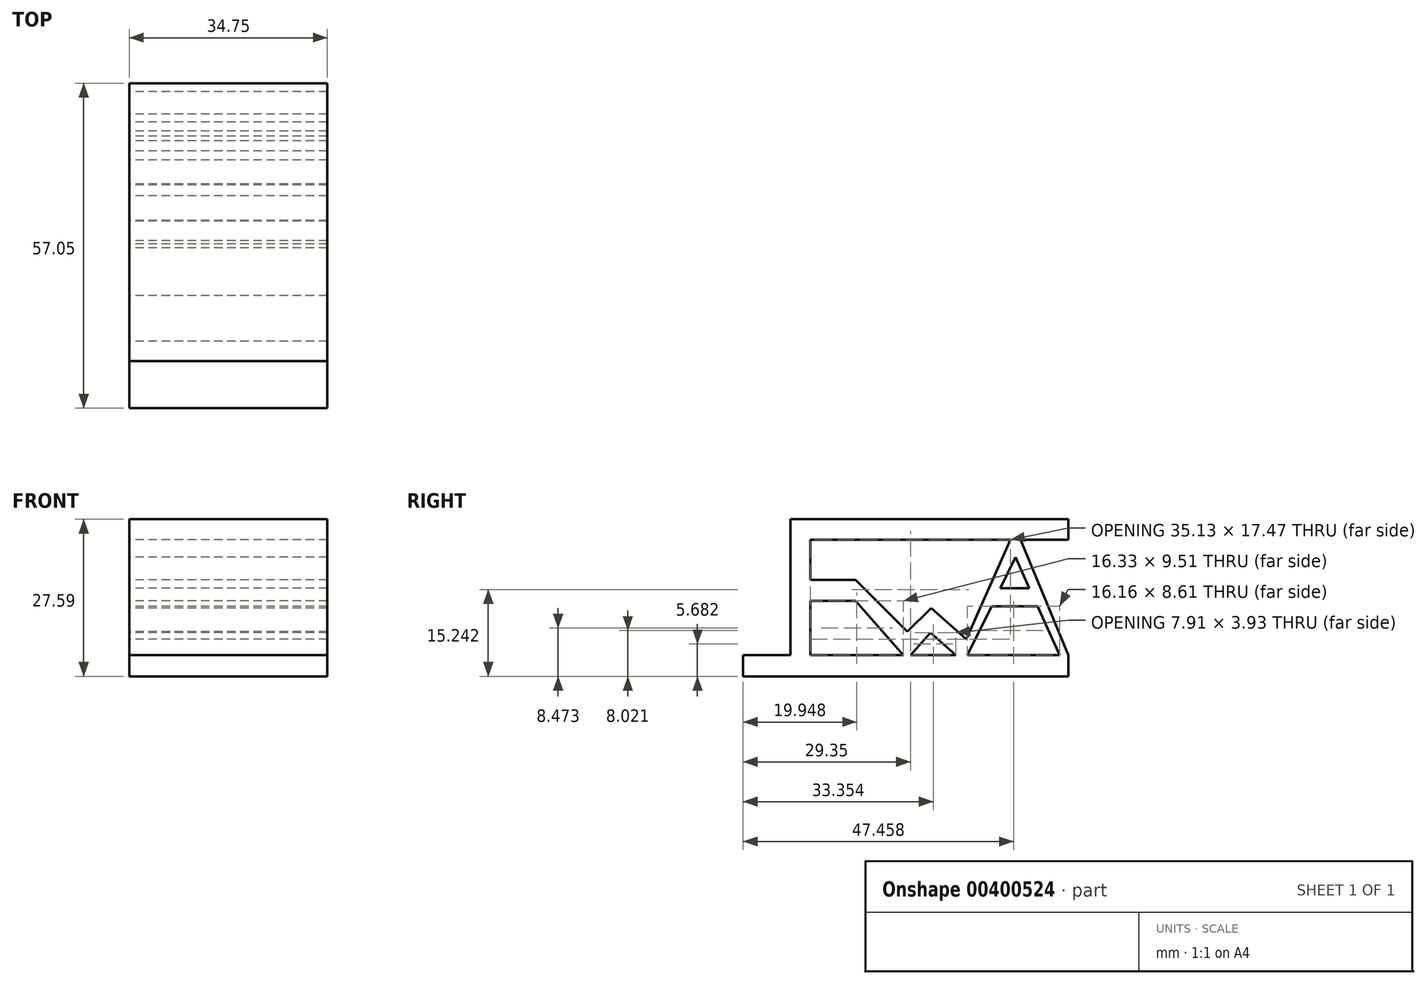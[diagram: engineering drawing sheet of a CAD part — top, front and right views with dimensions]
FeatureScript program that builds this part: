
annotation { "Feature Type Name" : "Feature", "Feature Type Description" : "" }
export const myFeature = defineFeature(function(context is Context, id is Id, definition is map)
    precondition{}
    {
        {
            var Q0;
            Q0=qCreatedBy(makeId("Right.planeOp"),FACE);
            var sketch = newSketch(context, id + "F0", { "sketchPlane" : qUnion([Q0])});
            skLineSegment(sketch, "E0.left", {"start": v(-48.05, 18.58) * mm, "end": v(-48.05, -25.84) * mm});
            skLineSegment(sketch, "E0.right", {"start": v(-40.34, 18.58) * mm, "end": v(-40.34, 3.17) * mm});
            skLineSegment(sketch, "E1.bottom", {"start": v(-40.34, 18.58) * mm, "end": v(36.7, 18.58) * mm});
            skLineSegment(sketch, "E1.top", {"start": v(-48.05, 26.52) * mm, "end": v(58.92, 26.52) * mm});
            skLineSegment(sketch, "E1.left", {"start": v(-48.05, 18.58) * mm, "end": v(-48.05, 26.52) * mm});
            skLineSegment(sketch, "E1.right", {"start": v(58.92, 18.58) * mm, "end": v(58.92, 26.52) * mm});
            skLineSegment(sketch, "E2.bottom", {"start": v(-40.34, 3.17) * mm, "end": v(-22.89, 3.17) * mm});
            skLineSegment(sketch, "E2.top", {"start": v(-40.34, -4.99) * mm, "end": v(-22.89, -4.99) * mm});
            skLineSegment(sketch, "E3.bottom", {"start": v(-66.18, -25.84) * mm, "end": v(-48.05, -25.84) * mm});
            skLineSegment(sketch, "E3.top", {"start": v(-66.18, -34) * mm, "end": v(58.92, -34) * mm});
            skLineSegment(sketch, "E3.left", {"start": v(-66.18, -25.84) * mm, "end": v(-66.18, -34) * mm});
            skLineSegment(sketch, "E3.right", {"start": v(58.92, -25.84) * mm, "end": v(58.92, -34) * mm});
            skPoint(sketch, "E4.middle", {"position": v(-22.89, -4.99) * mm});
            skLineSegment(sketch, "E5", {"start": v(38.59, 11.9) * mm, "end": v(32.78, 0) * mm});
            skLineSegment(sketch, "E6", {"start": v(38.59, 11.9) * mm, "end": v(43.96, 0) * mm});
            skLineSegment(sketch, "E7", {"start": v(-22.89, 3.17) * mm, "end": v(-2.95, -16.77) * mm});
            skLineSegment(sketch, "E8", {"start": v(15.64, -25.84) * mm, "end": v(5.9, -17.22) * mm});
            skLineSegment(sketch, "E9", {"start": v(-2.95, -16.77) * mm, "end": v(6.12, -7.7) * mm});
            skLineSegment(sketch, "E10", {"start": v(6.12, -7.7) * mm, "end": v(19.72, -19.72) * mm});
            skLineSegment(sketch, "E11", {"start": v(32.78, 0) * mm, "end": v(43.96, 0) * mm});
            skLineSegment(sketch, "E12", {"start": v(29.38, -6.96) * mm, "end": v(47.1, -6.96) * mm});
            skLineSegment(sketch, "E13.trimOffspring", {"start": v(47.1, -6.96) * mm, "end": v(55.61, -25.84) * mm});
            skLineSegment(sketch, "E14.trimOffspring", {"start": v(29.38, -6.96) * mm, "end": v(20.17, -25.84) * mm});
            skLineSegment(sketch, "E15.trimOffspring", {"start": v(-40.34, -4.99) * mm, "end": v(-40.34, -25.84) * mm});
            skLineSegment(sketch, "E16.trimOffspring", {"start": v(-40.34, -25.84) * mm, "end": v(-4.54, -25.84) * mm});
            skLineSegment(sketch, "E17", {"start": v(19.72, -19.72) * mm, "end": v(36.7, 18.58) * mm});
            skLineSegment(sketch, "E18", {"start": v(58.92, -25.84) * mm, "end": v(40.55, 18.58) * mm});
            skLineSegment(sketch, "E19.trimOffspring", {"start": v(40.55, 18.58) * mm, "end": v(58.92, 18.58) * mm});
            skLineSegment(sketch, "E20", {"start": v(5.9, -17.22) * mm, "end": v(-1.72, -25.84) * mm});
            skLineSegment(sketch, "E21", {"start": v(-22.89, -4.99) * mm, "end": v(-4.54, -25.84) * mm});
            skLineSegment(sketch, "E22.trimOffspring", {"start": v(-1.72, -25.84) * mm, "end": v(15.64, -25.84) * mm});
            skLineSegment(sketch, "E23.trimOffspring", {"start": v(20.17, -25.84) * mm, "end": v(55.61, -25.84) * mm});
            skSolve(sketch);
        }
        {
            var Q0;
            Q0=makeQuery(id+"F0.imprint","IMPRINT",FACE,{"disambiguationData":[TD([[makeQuery(id+"F0.imprint","IMPRINT",EDGE,{"derivedFrom":sQuery(id+"F0.wireOp",EDGE,"E0.left")}),1.0]])]});
            extrude(context, id + "F1", {"entities" : qUnion([Q0]), "depth" : 76.2 * mm});
        }
        {
            var Q0;
            Q0=makeQuery(id+"F1.opExtrude","SWEPT_BODY",BODY,{"disambiguationData":[OSD([sQuery(id+"F0.wireOp",EDGE,"E0.left"),sQuery(id+"F0.wireOp",EDGE,"E0.right"),sQuery(id+"F0.wireOp",EDGE,"E1.bottom"),sQuery(id+"F0.wireOp",EDGE,"E1.top"),sQuery(id+"F0.wireOp",EDGE,"E1.left"),sQuery(id+"F0.wireOp",EDGE,"E1.right"),sQuery(id+"F0.wireOp",EDGE,"E2.bottom"),sQuery(id+"F0.wireOp",EDGE,"E2.top"),sQuery(id+"F0.wireOp",EDGE,"E3.bottom"),sQuery(id+"F0.wireOp",EDGE,"E3.top"),sQuery(id+"F0.wireOp",EDGE,"E3.left"),sQuery(id+"F0.wireOp",EDGE,"E3.right"),sQuery(id+"F0.wireOp",EDGE,"E5"),sQuery(id+"F0.wireOp",EDGE,"E6"),sQuery(id+"F0.wireOp",EDGE,"E7"),sQuery(id+"F0.wireOp",EDGE,"E8"),sQuery(id+"F0.wireOp",EDGE,"E9"),sQuery(id+"F0.wireOp",EDGE,"E10"),sQuery(id+"F0.wireOp",EDGE,"E11"),sQuery(id+"F0.wireOp",EDGE,"E12"),sQuery(id+"F0.wireOp",EDGE,"E13.trimOffspring"),sQuery(id+"F0.wireOp",EDGE,"E14.trimOffspring"),sQuery(id+"F0.wireOp",EDGE,"E15.trimOffspring"),sQuery(id+"F0.wireOp",EDGE,"E16.trimOffspring"),sQuery(id+"F0.wireOp",EDGE,"E17"),sQuery(id+"F0.wireOp",EDGE,"E18"),sQuery(id+"F0.wireOp",EDGE,"E19.trimOffspring"),sQuery(id+"F0.wireOp",EDGE,"E20"),sQuery(id+"F0.wireOp",EDGE,"E21"),sQuery(id+"F0.wireOp",EDGE,"E22.trimOffspring"),sQuery(id+"F0.wireOp",EDGE,"E23.trimOffspring")])]});
            var Q1;
            Q1=qCreatedBy(makeId("Origin.pointOp"),VERTEX);
            transform(context, id + "F2", {"entities" : qUnion([Q0]), "transformType" : TransformType.SCALE_UNIFORMLY, "scale" : .456, "scalePoint" : qUnion([Q1]), "makeCopy" : false});
        }
    });
